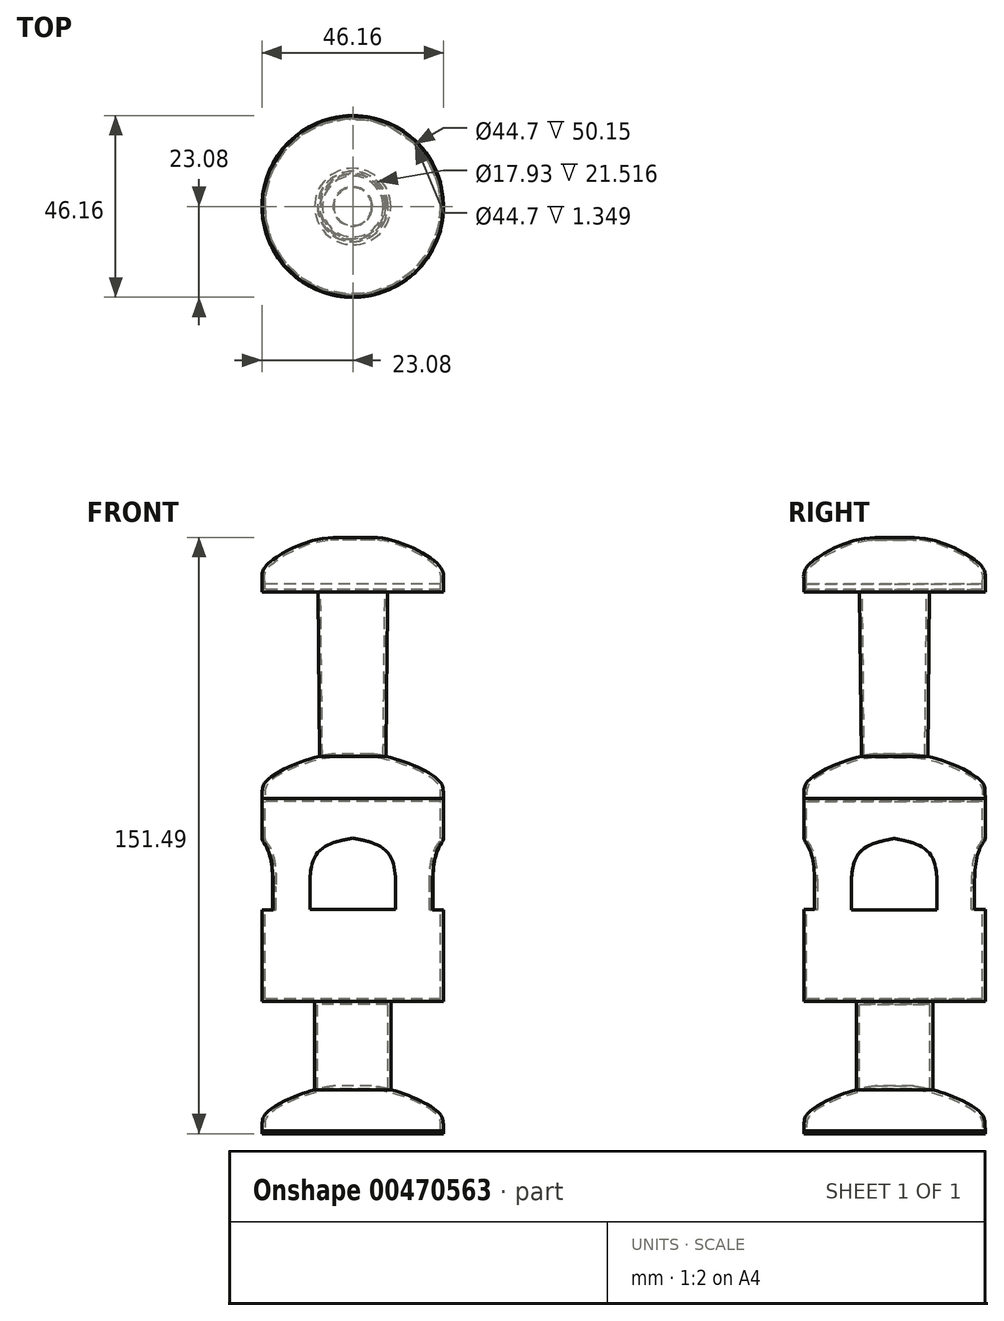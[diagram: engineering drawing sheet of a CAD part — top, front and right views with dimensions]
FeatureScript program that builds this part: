
annotation { "Feature Type Name" : "Feature", "Feature Type Description" : "" }
export const myFeature = defineFeature(function(context is Context, id is Id, definition is map)
    precondition{}
    {
        {
            var Q0;
            Q0=qCreatedBy(makeId("Front.planeOp"),FACE);
            var sketch = newSketch(context, id + "F0", { "sketchPlane" : qUnion([Q0])});
            skLineSegment(sketch, "E0", {"start": v(23.05, -27.33) * mm, "end": v(23.05, 24.18) * mm});
            skFitSpline(sketch, "E1", {"points": [v(23.05, 24.18) * mm, v(22.16, 28.47) * mm, v(4.82, 35.55) * mm], "startDerivative": vector(-1.43, 17.06) * mm, "endDerivative": vector(-27.68, 2.64) * mm});
            skLineSegment(sketch, "E2", {"start": v(22.35, -26.7) * mm, "end": v(22.35, 23.46) * mm});
            skFitSpline(sketch, "E3", {"points": [v(22.35, 23.46) * mm, v(21.6, 27.98) * mm, v(4.86, 34.7) * mm], "startDerivative": vector(-1.43, 17.06) * mm, "endDerivative": vector(-27.68, 2.64) * mm});
            skLineSegment(sketch, "E4", {"start": v(22.35, -26.7) * mm, "end": v(0, -26.7) * mm});
            skLineSegment(sketch, "E5", {"start": v(22.35, 23.04) * mm, "end": v(23.05, 23.04) * mm, "construction": true});
            skLineSegment(sketch, "E6", {"start": v(6.55, -26.7) * mm, "end": v(6.55, -27.4) * mm, "construction": true});
            skLineSegment(sketch, "E7", {"start": v(0, -26.7) * mm, "end": v(0, -27.42) * mm});
            skLineSegment(sketch, "E8", {"start": v(0, -27.42) * mm, "end": v(18.83, -27.35) * mm});
            skLineSegment(sketch, "E9", {"start": v(20.28, -27.34) * mm, "end": v(23.05, -27.33) * mm});
            skLineSegment(sketch, "E10", {"start": v(0, 35.55) * mm, "end": v(0, -49.7) * mm, "construction": true});
            skLineSegment(sketch, "E11", {"start": v(0, -27.42) * mm, "end": v(23.05, -27.33) * mm});
            skLineSegment(sketch, "E12", {"start": v(4.82, 35.55) * mm, "end": v(0, 35.55) * mm});
            skLineSegment(sketch, "E13", {"start": v(0, 35.55) * mm, "end": v(0, 34.7) * mm});
            skLineSegment(sketch, "E14", {"start": v(0, 34.7) * mm, "end": v(4.86, 34.7) * mm});
            skLineSegment(sketch, "E15", {"start": v(2.05, 35.55) * mm, "end": v(2.05, 34.7) * mm, "construction": true});
            skFitSpline(sketch, "E16", {"points": [v(23.05, -60.22) * mm, v(22.16, -55.92) * mm, v(4.82, -48.84) * mm], "startDerivative": vector(-1.43, 17.06) * mm, "endDerivative": vector(-27.68, 2.64) * mm});
            skFitSpline(sketch, "E17", {"points": [v(22.35, -60.94) * mm, v(21.6, -56.41) * mm, v(4.86, -49.7) * mm], "startDerivative": vector(-1.43, 17.06) * mm, "endDerivative": vector(-27.68, 2.64) * mm});
            skLineSegment(sketch, "E18", {"start": v(4.82, -48.84) * mm, "end": v(0, -48.84) * mm});
            skLineSegment(sketch, "E19", {"start": v(0, -48.84) * mm, "end": v(0, -49.7) * mm});
            skLineSegment(sketch, "E20", {"start": v(0, -49.7) * mm, "end": v(4.86, -49.7) * mm});
            skLineSegment(sketch, "E21", {"start": v(2.05, -48.84) * mm, "end": v(2.05, -49.7) * mm, "construction": true});
            skLineSegment(sketch, "E22", {"start": v(23.05, -60.22) * mm, "end": v(23.05, -60.94) * mm});
            skLineSegment(sketch, "E23", {"start": v(23.05, -60.94) * mm, "end": v(22.35, -60.94) * mm});
            skLineSegment(sketch, "E24", {"start": v(0, -37.24) * mm, "end": v(9, -37.24) * mm, "construction": true});
            skLineSegment(sketch, "E25", {"start": v(9, -33.53) * mm, "end": v(9.7, -33.53) * mm, "construction": true});
            skLineSegment(sketch, "E26", {"start": v(8.96, -27.39) * mm, "end": v(8.96, -49.59) * mm});
            skLineSegment(sketch, "E27", {"start": v(9.7, -49.59) * mm, "end": v(9.7, -27.38) * mm});
            skLineSegment(sketch, "E28", {"start": v(9.7, -49.59) * mm, "end": v(9.7, -49.78) * mm});
            skLineSegment(sketch, "E29", {"start": v(22.35, -60.94) * mm, "end": v(0, -60.94) * mm});
            skLineSegment(sketch, "E30", {"start": v(0, -60.94) * mm, "end": v(0, -60.23) * mm});
            skLineSegment(sketch, "E31", {"start": v(0, -60.23) * mm, "end": v(22.32, -60.23) * mm});
            skLineSegment(sketch, "E32", {"start": v(8.96, -28.07) * mm, "end": v(0, -28.07) * mm});
            skLineSegment(sketch, "E33", {"start": v(0, -28.07) * mm, "end": v(0, -27.42) * mm});
            skLineSegment(sketch, "E34", {"start": v(0, -48.84) * mm, "end": v(0, -60.94) * mm, "construction": true});
            skFitSpline(sketch, "E35", {"points": [v(23.05, 78.72) * mm, v(22.16, 83.17) * mm, v(5, 90.55) * mm], "startDerivative": vector(0, 17.12) * mm, "endDerivative": vector(-27.8, 0) * mm});
            skLineSegment(sketch, "E36", {"start": v(5, 90.55) * mm, "end": v(0, 90.55) * mm});
            skLineSegment(sketch, "E37.bottom", {"start": v(23.05, 78.72) * mm, "end": v(23.05, 78.72) * mm});
            skLineSegment(sketch, "E37.top", {"start": v(23.05, 76.67) * mm, "end": v(23.05, 76.67) * mm});
            skLineSegment(sketch, "E37.left", {"start": v(23.05, 78.72) * mm, "end": v(23.05, 76.67) * mm});
            skLineSegment(sketch, "E37.right", {"start": v(23.05, 78.72) * mm, "end": v(23.05, 76.67) * mm});
            skLineSegment(sketch, "E38", {"start": v(23.05, 76.67) * mm, "end": v(8.87, 76.67) * mm});
            skLineSegment(sketch, "E39", {"start": v(8.87, 76.67) * mm, "end": v(8.42, 34.94) * mm});
            skLineSegment(sketch, "E40", {"start": v(0, 96.04) * mm, "end": v(0, 29.02) * mm, "construction": true});
            skLineSegment(sketch, "E41", {"start": v(0, 36.25) * mm, "end": v(0, 35.55) * mm});
            skLineSegment(sketch, "E42.0", {"start": v(5, 89.85) * mm, "end": v(0, 89.85) * mm});
            skLineSegment(sketch, "E42.1", {"start": v(8.17, 77.37) * mm, "end": v(7.72, 35.1) * mm});
            skLineSegment(sketch, "E42.2", {"start": v(22.35, 77.37) * mm, "end": v(8.17, 77.37) * mm});
            skLineSegment(sketch, "E42.3", {"start": v(22.35, 78.72) * mm, "end": v(22.35, 77.37) * mm});
            skFitSpline(sketch, "E42.4", {"points": [v(22.35, 78.72) * mm, v(22.35, 79.1) * mm, v(22.37, 79.77) * mm, v(22.4, 80.6) * mm, v(22.34, 81.28) * mm, v(22.17, 81.88) * mm, v(21.88, 82.4) * mm, v(21.5, 82.89) * mm, v(21, 83.41) * mm, v(20.17, 84.13) * mm, v(18.93, 85.03) * mm, v(17.47, 85.93) * mm, v(15.3, 87.1) * mm, v(12.27, 88.43) * mm, v(8.48, 89.56) * mm, v(6.1, 89.85) * mm, v(5, 89.85) * mm]});
            skLineSegment(sketch, "E43", {"start": v(0, 90.55) * mm, "end": v(0, 89.85) * mm});
            skSolve(sketch);
        }
        {
            var Q0;
            {var subQ6=sQuery(id+"F0.wireOp",EDGE,"E0");Q0=makeQuery(id+"F0.imprint","IMPRINT",FACE,{"disambiguationData":[TD([[makeQuery(id+"F0.imprint","IMPRINT",EDGE,{"derivedFrom":subQ6}),1.0]])]});}
            var Q1;
            Q1=sQuery(id+"F0.wireOp",EDGE,"E10");
            revolve(context, id + "F1", {"entities" : qUnion([Q0]), "axis" : qUnion([Q1]), "revolveType" : RevolveType.FULL});
        }
        {
            var Q0;
            {var subQ3=sQuery(id+"F0.wireOp",EDGE,"E18");Q0=makeQuery(id+"F0.imprint","IMPRINT",FACE,{"disambiguationData":[TD([[makeQuery(id+"F0.imprint","IMPRINT",EDGE,{"derivedFrom":subQ3}),1.0]])]});}
            var Q1;
            {var subQ5=sQuery(id+"F0.wireOp",EDGE,"E27");Q1=makeQuery(id+"F0.imprint","IMPRINT",FACE,{"disambiguationData":[TD([[makeQuery(id+"F0.imprint","IMPRINT",EDGE,{"derivedFrom":subQ5}),1.0]])]});}
            var Q2;
            {var subQ0=sQuery(id+"F0.wireOp",EDGE,"E29");Q2=makeQuery(id+"F0.imprint","IMPRINT",FACE,{"disambiguationData":[TD([[makeQuery(id+"F0.imprint","IMPRINT",EDGE,{"derivedFrom":subQ0}),-1.0]])]});}
            var Q3;
            {var subQ4=sQuery(id+"F0.wireOp",EDGE,"E32");Q3=makeQuery(id+"F0.imprint","IMPRINT",FACE,{"disambiguationData":[TD([[makeQuery(id+"F0.imprint","IMPRINT",EDGE,{"derivedFrom":subQ4}),-1.0]])]});}
            var Q4;
            Q4=sQuery(id+"F0.wireOp",EDGE,"E10");
            revolve(context, id + "F2", {"operationType" : NewBodyOperationType.ADD, "entities" : qUnion([Q0, Q1, Q2, Q3]), "axis" : qUnion([Q4]), "revolveType" : RevolveType.FULL});
        }
        {
            var Q0;
            Q0=qCreatedBy(makeId("Right.planeOp"),FACE);
            var sketch = newSketch(context, id + "F3", { "sketchPlane" : qUnion([Q0])});
            skLineSegment(sketch, "E44", {"start": v(-0.1, -4.1) * mm, "end": v(10.78, -4.1) * mm});
            skLineSegment(sketch, "E45", {"start": v(10.78, -4.1) * mm, "end": v(10.78, 1.7) * mm});
            skFitSpline(sketch, "E46", {"points": [v(10.78, 1.7) * mm, v(-0.1, 14.05) * mm], "startDerivative": vector(0.33, 26.9) * mm, "endDerivative": vector(-25.41, 4.6) * mm});
            skFitSpline(sketch, "E47.MirrorCS", {"points": [v(-10.97, 1.7) * mm, v(-0.1, 14.05) * mm], "startDerivative": vector(-0.33, 26.9) * mm, "endDerivative": vector(25.41, 4.6) * mm});
            skLineSegment(sketch, "E48.MirrorCS", {"start": v(-10.97, -4.1) * mm, "end": v(-10.97, 1.7) * mm});
            skLineSegment(sketch, "E49.MirrorCS", {"start": v(-0.1, -4.1) * mm, "end": v(-10.97, -4.1) * mm});
            skSolve(sketch);
        }
        {
            var Q0;
            Q0=makeQuery(id+"F3.imprint","IMPRINT",FACE,{"disambiguationData":[TD([[makeQuery(id+"F3.imprint","IMPRINT",EDGE,{"derivedFrom":sQuery(id+"F3.wireOp",EDGE,"E44")}),1.0]])]});
            extrude(context, id + "F4", {"entities" : qUnion([Q0]), "operationType" : NewBodyOperationType.REMOVE, "endBound" : BoundingType.SYMMETRIC, "depth" : 50 * mm});
        }
        {
            var Q0;
            Q0=qCreatedBy(makeId("Front.planeOp"),FACE);
            var sketch = newSketch(context, id + "F5", { "sketchPlane" : qUnion([Q0])});
            skLineSegment(sketch, "E50", {"start": v(0, -4) * mm, "end": v(10.87, -4) * mm});
            skLineSegment(sketch, "E51", {"start": v(10.87, -4) * mm, "end": v(10.87, 1.8) * mm});
            skFitSpline(sketch, "E52", {"points": [v(10.87, 1.8) * mm, v(0, 14.15) * mm], "startDerivative": vector(0.33, 26.9) * mm, "endDerivative": vector(-25.41, 4.6) * mm});
            skFitSpline(sketch, "E53.MirrorCS", {"points": [v(-10.88, 1.8) * mm, v(0, 14.15) * mm], "startDerivative": vector(-0.33, 26.9) * mm, "endDerivative": vector(25.41, 4.6) * mm});
            skLineSegment(sketch, "E54.MirrorCS", {"start": v(-10.88, -4) * mm, "end": v(-10.88, 1.8) * mm});
            skLineSegment(sketch, "E55.MirrorCS", {"start": v(0, -4) * mm, "end": v(-10.88, -4) * mm});
            skSolve(sketch);
        }
        {
            var Q0;
            Q0=makeQuery(id+"F5.imprint","IMPRINT",FACE,{"disambiguationData":[TD([[makeQuery(id+"F5.imprint","IMPRINT",EDGE,{"derivedFrom":sQuery(id+"F5.wireOp",EDGE,"E50")}),1.0]])]});
            extrude(context, id + "F6", {"entities" : qUnion([Q0]), "operationType" : NewBodyOperationType.REMOVE, "endBound" : BoundingType.SYMMETRIC, "depth" : 50 * mm});
        }
        {
            var Q0;
            Q0=makeQuery(id+"F0.imprint","IMPRINT",FACE,{"disambiguationData":[TD([[makeQuery(id+"F0.imprint","IMPRINT",EDGE,{"derivedFrom":sQuery(id+"F0.wireOp",EDGE,"E35")}),1.0]])]});
            var Q1;
            Q1=sQuery(id+"F0.wireOp",EDGE,"E40");
            revolve(context, id + "F7", {"operationType" : NewBodyOperationType.ADD, "entities" : qUnion([Q0]), "axis" : qUnion([Q1]), "revolveType" : RevolveType.FULL});
        }
    });
